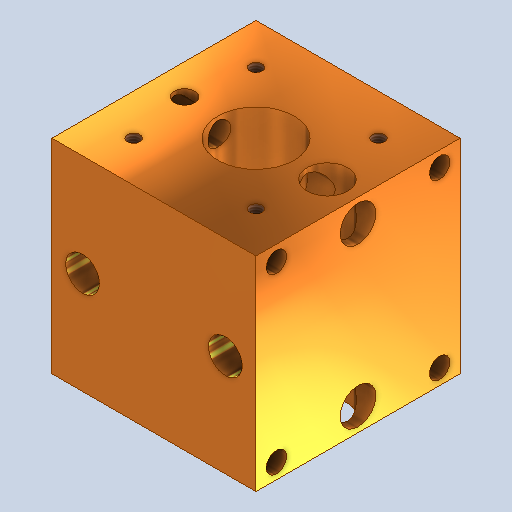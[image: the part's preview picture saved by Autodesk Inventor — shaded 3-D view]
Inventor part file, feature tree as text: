
AUTODESK INVENTOR PART (.ipt)
format: ipt  version: 2025.1 (Build 291241000, 241)  size: 391,680 bytes
history: native  units: mm
features: hole x10, sketch x6, extrude x1, plane x1, mirror x1
ambient origin geometry x8: Origin, YZ Plane, XZ Plane, XY Plane, X Axis, Y Axis, Z Axis, Center Point
bodies: Solid1 (feature_tree)
feature tree (19):
  extrude  "Extrusion1"  Depth=40.0mm
  sketch  "Sketch2"  dims[d2=40.0mm d3=0.0mm d5=14.0mm]
  hole  "Hole2"  [1 undecoded]
  hole  "Hole3"  [1 undecoded]
  hole  "Hole4"  [1 undecoded]
  sketch  "Sketch3"  dims[d6=28.0mm d7=24.0mm]
  hole  "Hole5"  [1 undecoded]
  hole  "Hole6"  [1 undecoded]
  hole  "Hole7"  [1 undecoded]
  sketch  "Sketch6"  dims[d10=12.0mm]
  hole  "Hole8"  [1 undecoded]
  hole  "Hole9"  [1 undecoded]
  hole  "Hole1"  [1 undecoded]
  hole  "Hole10"  [1 undecoded]
  plane  "Work Plane4"
  mirror  "Mirror1"
  sketch  "Sketch1"  dims[d0=40.0mm d1=40.0mm]
  sketch  "Sketch4"  dims[d8=12.0mm d9=24.0mm]
  sketch  "Sketch9"  dims[d11=15.0mm d12=6.0mm d13=4.0mm d14=2.0mm d15=90.0deg d16=8.0mm d17=0.0mm d18=4.0mm d19=6.0mm d20=4.0mm d21=2.0mm d22=90.0deg d23=15.0mm d24=0.0mm d25=2.459mm d26=6.0mm d27=4.0mm d28=2.0mm d29=90.0deg d30=8.0mm d31=0.0mm d32=8.0mm d33=6.0mm d34=4.0mm d35=2.0mm d36=90.0deg d37=8.0mm d38=0.0mm d39=20.0mm d40=4.5mm d41=31.0mm d42=32.0mm d43=16.0mm d44=34.0mm d45=17.0mm d46=7.0mm d47=6.0mm d48=4.0mm d49=2.0mm d50=90.0deg d51=20.0mm d52=0.0mm d53=4.0mm d54=6.0mm d55=4.0mm d56=2.0mm d57=90.0deg d58=20.0mm d59=0.0mm d60=6.0mm d61=6.0mm d62=6.647mm d63=16.0mm d64=4.0mm d65=2.0mm d66=90.0deg d67=8.0mm d68=0.0mm d69=16.0mm d70=8.0mm d71=6.0mm d72=16.0mm d73=4.0mm d74=2.0mm d75=90.0deg d76=20.0mm d77=0.0mm d78=4.0mm d79=6.0mm d80=4.0mm d81=2.0mm d82=90.0deg d83=20.0mm d84=0.0mm d87=4.5mm d88=6.0mm d89=4.0mm d90=2.0mm d91=90.0deg d92=15.0mm d93=0.0mm d95=20.0mm]
note: 10 required parameter values undecoded (feature->parameter linkage not recoverable at this tier; creation-order binding heuristic only, values carry confidence <= 0.55)
